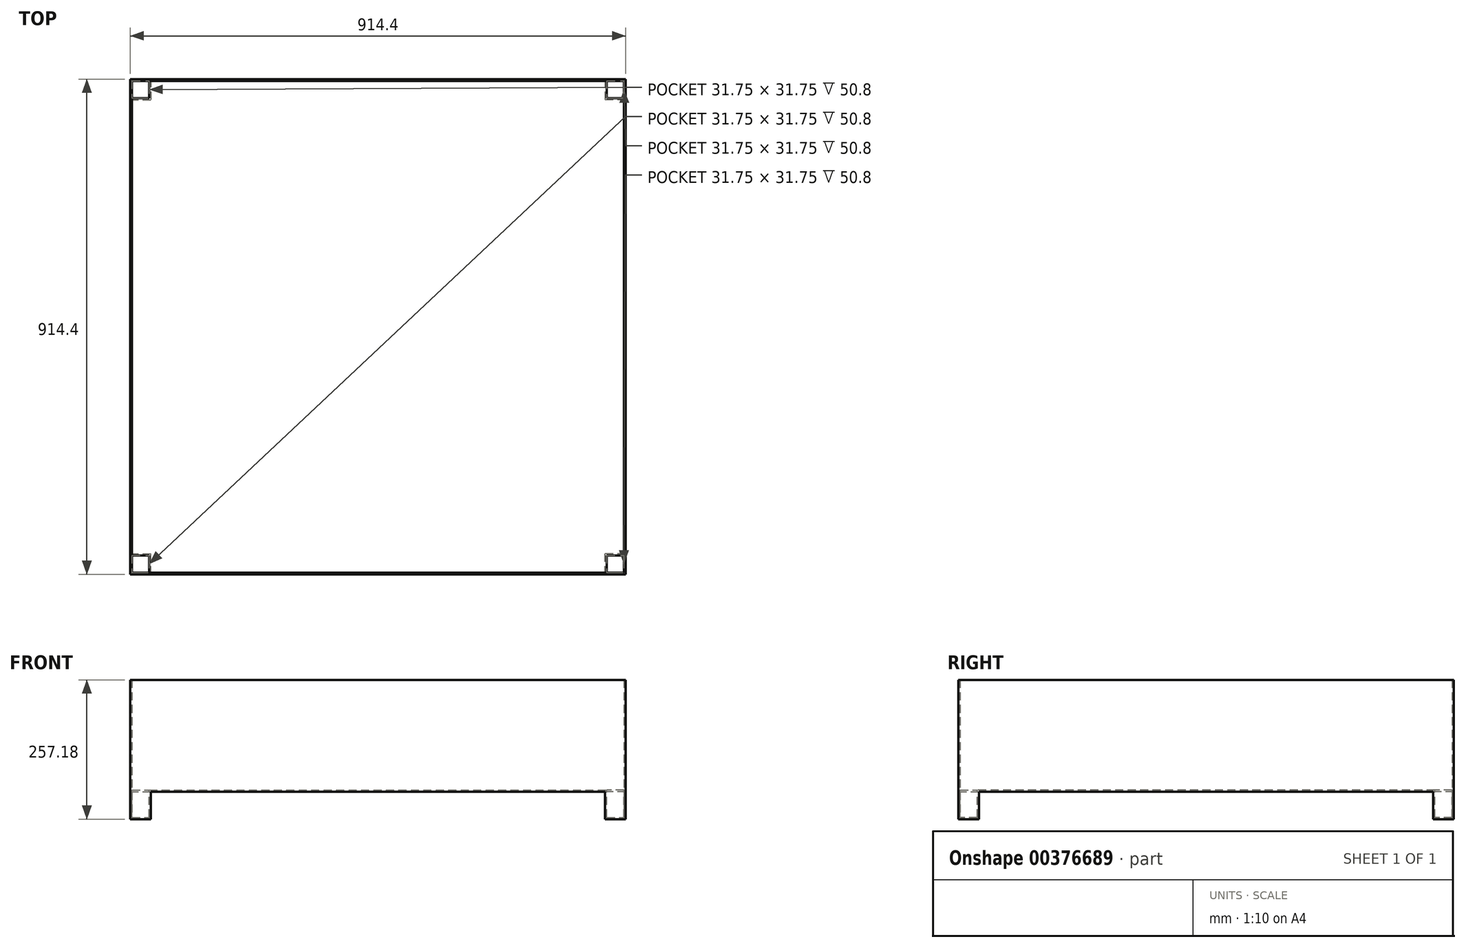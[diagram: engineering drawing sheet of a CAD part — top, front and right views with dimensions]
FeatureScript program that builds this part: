
annotation { "Feature Type Name" : "Feature", "Feature Type Description" : "" }
export const myFeature = defineFeature(function(context is Context, id is Id, definition is map)
    precondition{}
    {
        {
            var Q0;
            Q0=qCreatedBy(makeId("Top.planeOp"),FACE);
            var sketch = newSketch(context, id + "F0", { "sketchPlane" : qUnion([Q0])});
            skLineSegment(sketch, "E0.bottom", {"start": v(-457.2, 457.2) * mm, "end": v(457.2, 457.2) * mm});
            skLineSegment(sketch, "E0.top", {"start": v(-457.2, -457.2) * mm, "end": v(457.2, -457.2) * mm});
            skLineSegment(sketch, "E0.left", {"start": v(-457.2, 457.2) * mm, "end": v(-457.2, -457.2) * mm});
            skLineSegment(sketch, "E0.right", {"start": v(457.2, 457.2) * mm, "end": v(457.2, -457.2) * mm});
            skPoint(sketch, "E0.middle", {"position": v(0, 0) * mm});
            skSolve(sketch);
        }
        {
            var Q0;
            Q0=makeQuery(id+"F0.imprint","IMPRINT",FACE,{"disambiguationData":[TD([[makeQuery(id+"F0.imprint","IMPRINT",EDGE,{"derivedFrom":sQuery(id+"F0.wireOp",EDGE,"E0.bottom")}),-1.0]])]});
            extrude(context, id + "F1", {"entities" : qUnion([Q0]), "depth" : 3.17 * mm});
        }
        {
            var Q0;
            Q0=makeQuery(id+"F1.opExtrude","CAP_FACE",FACE,{"disambiguationData":[OSD([sQuery(id+"F0.wireOp",EDGE,"E0.bottom"),sQuery(id+"F0.wireOp",EDGE,"E0.top"),sQuery(id+"F0.wireOp",EDGE,"E0.left"),sQuery(id+"F0.wireOp",EDGE,"E0.right")])],"isStart":false});
            var sketch = newSketch(context, id + "F2", { "sketchPlane" : qUnion([Q0])});
            skLineSegment(sketch, "E1.0.0", {"start": v(-457.2, 457.2) * mm, "end": v(-457.2, -457.2) * mm});
            skLineSegment(sketch, "E1.0.1", {"start": v(-457.2, -457.2) * mm, "end": v(457.2, -457.2) * mm});
            skLineSegment(sketch, "E1.0.2", {"start": v(457.2, -457.2) * mm, "end": v(457.2, 457.2) * mm});
            skLineSegment(sketch, "E1.0.3", {"start": v(457.2, 457.2) * mm, "end": v(-457.2, 457.2) * mm});
            skLineSegment(sketch, "E2.0", {"start": v(454.03, 454.03) * mm, "end": v(-454.02, 454.03) * mm});
            skLineSegment(sketch, "E2.1", {"start": v(454.02, -454.03) * mm, "end": v(454.03, 454.03) * mm});
            skLineSegment(sketch, "E2.2", {"start": v(-454.03, -454.03) * mm, "end": v(454.02, -454.03) * mm});
            skLineSegment(sketch, "E2.3", {"start": v(-454.02, 454.03) * mm, "end": v(-454.03, -454.03) * mm});
            skSolve(sketch);
        }
        {
            var Q0;
            Q0=makeQuery(id+"F2.imprint","IMPRINT",FACE,{"disambiguationData":[TD([[makeQuery(id+"F2.imprint","IMPRINT",EDGE,{"derivedFrom":sQuery(id+"F2.wireOp",EDGE,"E1.0.0")}),1.0]])]});
            var Q1;
            Q1=makeQuery(id+"F2.imprint","IMPRINT",FACE,{"disambiguationData":[TD([[makeQuery(id+"F2.imprint","IMPRINT",EDGE,{"derivedFrom":sQuery(id+"F2.wireOp",EDGE,"E2.0")}),1.0]])]});
            extrude(context, id + "F3", {"entities" : qUnion([Q0, Q1]), "operationType" : NewBodyOperationType.ADD, "depth" : 203.2 * mm});
        }
        {
            var Q0;
            Q0=makeQuery(id+"F1.opExtrude","CAP_FACE",FACE,{"disambiguationData":[OSD([sQuery(id+"F0.wireOp",EDGE,"E0.bottom"),sQuery(id+"F0.wireOp",EDGE,"E0.top"),sQuery(id+"F0.wireOp",EDGE,"E0.left"),sQuery(id+"F0.wireOp",EDGE,"E0.right")])],"isStart":true});
            var sketch = newSketch(context, id + "F4", { "sketchPlane" : qUnion([Q0])});
            skLineSegment(sketch, "E3.bottom", {"start": v(-457.2, -457.2) * mm, "end": v(-419.1, -457.2) * mm});
            skLineSegment(sketch, "E3.top", {"start": v(-457.2, -419.1) * mm, "end": v(-419.1, -419.1) * mm});
            skLineSegment(sketch, "E3.left", {"start": v(-457.2, -457.2) * mm, "end": v(-457.2, -419.1) * mm});
            skLineSegment(sketch, "E3.right", {"start": v(-419.1, -457.2) * mm, "end": v(-419.1, -419.1) * mm});
            skLineSegment(sketch, "E4.MirrorCS", {"start": v(-419.1, 457.2) * mm, "end": v(-419.1, 419.1) * mm});
            skLineSegment(sketch, "E5.MirrorCS", {"start": v(-457.2, 457.2) * mm, "end": v(-457.2, 419.1) * mm});
            skLineSegment(sketch, "E6.MirrorCS", {"start": v(-457.2, 457.2) * mm, "end": v(-419.1, 457.2) * mm});
            skLineSegment(sketch, "E7.MirrorCS", {"start": v(-457.2, 419.1) * mm, "end": v(-419.1, 419.1) * mm});
            skLineSegment(sketch, "E8.MirrorCS", {"start": v(457.2, -457.2) * mm, "end": v(457.2, -419.1) * mm});
            skLineSegment(sketch, "E9.MirrorCS", {"start": v(457.2, -457.2) * mm, "end": v(419.1, -457.2) * mm});
            skLineSegment(sketch, "E10.MirrorCS", {"start": v(419.1, -457.2) * mm, "end": v(419.1, -419.1) * mm});
            skLineSegment(sketch, "E11.MirrorCS", {"start": v(457.2, -419.1) * mm, "end": v(419.1, -419.1) * mm});
            skLineSegment(sketch, "E12.MirrorCS", {"start": v(419.1, 457.2) * mm, "end": v(419.1, 419.1) * mm});
            skLineSegment(sketch, "E13.MirrorCS", {"start": v(457.2, 419.1) * mm, "end": v(419.1, 419.1) * mm});
            skLineSegment(sketch, "E14.MirrorCS", {"start": v(457.2, 457.2) * mm, "end": v(457.2, 419.1) * mm});
            skLineSegment(sketch, "E15.MirrorCS", {"start": v(457.2, 457.2) * mm, "end": v(419.1, 457.2) * mm});
            skSolve(sketch);
        }
        {
            var Q0;
            Q0=makeQuery(id+"F4.imprint","IMPRINT",FACE,{"disambiguationData":[TD([[makeQuery(id+"F4.imprint","IMPRINT",EDGE,{"derivedFrom":sQuery(id+"F4.wireOp",EDGE,"E3.bottom")}),1.0]])]});
            var Q1;
            Q1=makeQuery(id+"F4.imprint","IMPRINT",FACE,{"disambiguationData":[TD([[makeQuery(id+"F4.imprint","IMPRINT",EDGE,{"derivedFrom":sQuery(id+"F4.wireOp",EDGE,"E8.MirrorCS")}),1.0]])]});
            var Q2;
            Q2=makeQuery(id+"F4.imprint","IMPRINT",FACE,{"disambiguationData":[TD([[makeQuery(id+"F4.imprint","IMPRINT",EDGE,{"derivedFrom":sQuery(id+"F4.wireOp",EDGE,"E12.MirrorCS")}),1.0]])]});
            var Q3;
            Q3=makeQuery(id+"F4.imprint","IMPRINT",FACE,{"disambiguationData":[TD([[makeQuery(id+"F4.imprint","IMPRINT",EDGE,{"derivedFrom":sQuery(id+"F4.wireOp",EDGE,"E6.MirrorCS")}),-1.0]])]});
            extrude(context, id + "F5", {"entities" : qUnion([Q0, Q1, Q2, Q3]), "operationType" : NewBodyOperationType.ADD, "depth" : 50.8 * mm});
        }
        {
            var Q0;
            Q0=makeQuery(id+"F3.opExtrude","CAP_FACE",FACE,{"disambiguationData":[OSD([sQuery(id+"F2.wireOp",EDGE,"E1.0.0"),sQuery(id+"F2.wireOp",EDGE,"E1.0.1"),sQuery(id+"F2.wireOp",EDGE,"E1.0.2"),sQuery(id+"F2.wireOp",EDGE,"E1.0.3")])],"isStart":false});
            shell(context, id + "F6", {"entities" : qUnion([Q0]), "thickness" : 3.17 * mm});
        }
    });
